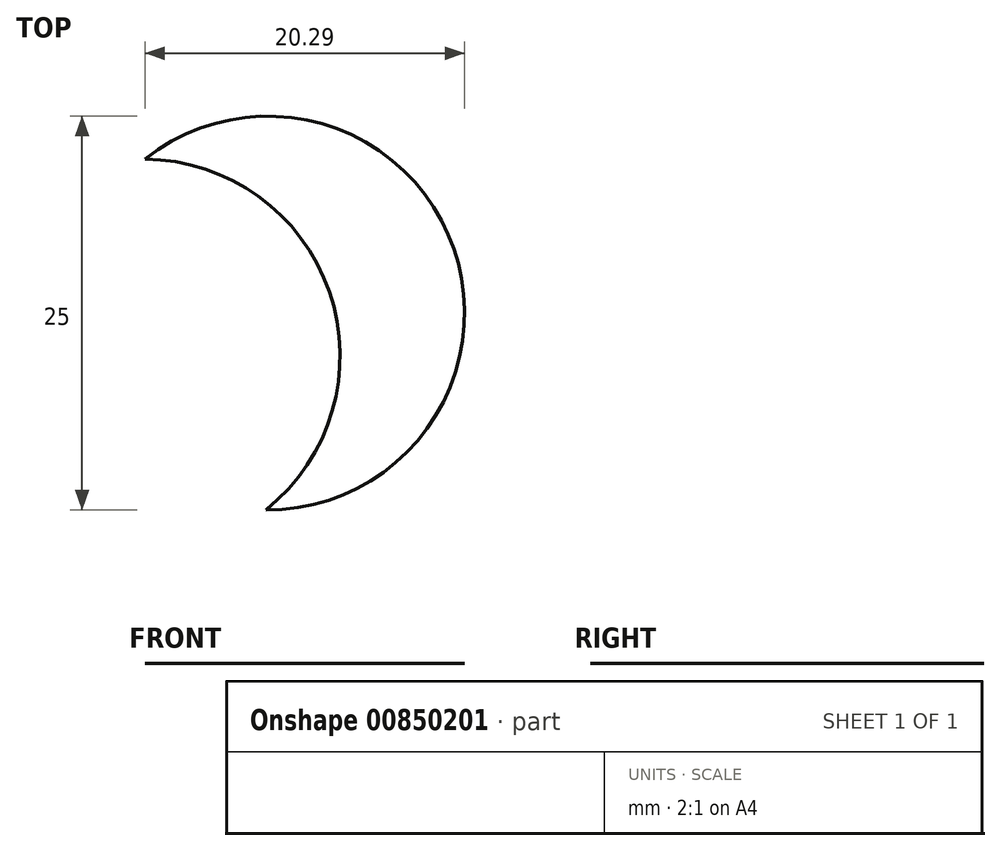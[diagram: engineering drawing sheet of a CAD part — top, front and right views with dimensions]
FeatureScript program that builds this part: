
annotation { "Feature Type Name" : "Feature", "Feature Type Description" : "" }
export const myFeature = defineFeature(function(context is Context, id is Id, definition is map)
    precondition{}
    {
        {
            var Q0;
            Q0=qCreatedBy(makeId("Top.planeOp"),FACE);
            var sketch = newSketch(context, id + "F0", { "sketchPlane" : qUnion([Q0])});
            skCircle(sketch, "E0", {"center": v(164.3, 0) * mm, "radius": 12.5 * mm});
            skCircle(sketch, "E1", {"center": v(156.39, -2.73) * mm, "radius": 12.5 * mm});
            skSolve(sketch);
        }
        {
            var Q0;
            {var subQ0=sQuery(id+"F0.wireOp",EDGE,"E1");var subQ1=sQuery(id+"F0.wireOp",EDGE,"E0");var subQ2=makeQuery(id+"F0.imprint","INTERSECT",VERTEX,{"disambiguationData":[OD(0.0)],"derivedFrom":[subQ1,subQ0]});Q0=makeQuery(id+"F0.imprint","IMPRINT",FACE,{"disambiguationData":[TD([[makeQuery(id+"F0.imprint","IMPRINT",EDGE,{"disambiguationData":[TD([[subQ2,-1.0]])],"derivedFrom":subQ1}),1.0]])]});}
            var sketch = newSketch(context, id + "F1", { "sketchPlane" : qUnion([Q0])});
            skSolve(sketch);
        }
        {
            var Q0;
            {var subQ0=sQuery(id+"F0.wireOp",EDGE,"E1");var subQ1=sQuery(id+"F0.wireOp",EDGE,"E0");var subQ2=makeQuery(id+"F0.imprint","INTERSECT",VERTEX,{"disambiguationData":[OD(0.0)],"derivedFrom":[subQ1,subQ0]});Q0=makeQuery(id+"F1.imprint","IMPRINT",FACE,{"disambiguationData":[TD([[makeQuery(id+"F1.imprint","IMPRINT",EDGE,{"derivedFrom":makeQuery(id+"F0.imprint","IMPRINT",EDGE,{"disambiguationData":[TD([[subQ2,-1.0]])],"derivedFrom":subQ1})}),1.0]])]});}
            extrude(context, id + "F2", {"entities" : qUnion([Q0]), "depth" : 1 / 406.4 * mm, "offsetDistance" : 25.4 * mm});
        }
    });
